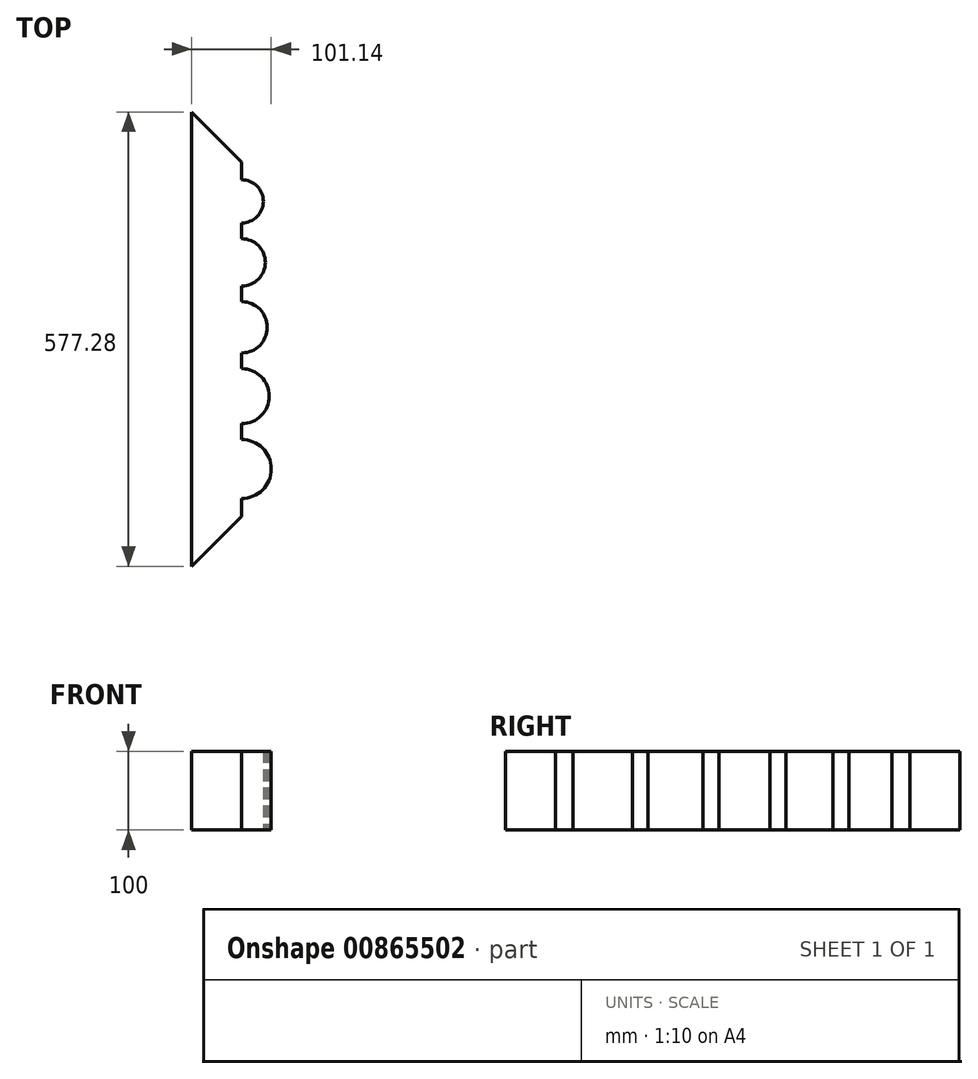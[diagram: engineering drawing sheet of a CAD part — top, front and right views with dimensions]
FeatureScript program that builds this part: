
annotation { "Feature Type Name" : "Feature", "Feature Type Description" : "" }
export const myFeature = defineFeature(function(context is Context, id is Id, definition is map)
    precondition{}
    {
        {
            var Q0;
            Q0=qCreatedBy(makeId("Top.planeOp"),FACE);
            var sketch = newSketch(context, id + "F0", { "sketchPlane" : qUnion([Q0])});
            skLineSegment(sketch, "E0.bottom", {"start": v(0, 0) * mm, "end": v(450, 0) * mm});
            skLineSegment(sketch, "E0.top", {"start": v(0, -450) * mm, "end": v(450, -450) * mm});
            skLineSegment(sketch, "E0.left", {"start": v(0, 0) * mm, "end": v(0, -450) * mm});
            skLineSegment(sketch, "E0.right", {"start": v(450, 0) * mm, "end": v(450, -450) * mm});
            skCircle(sketch, "E1", {"center": v(32.5, 0) * mm, "radius": 7.5 * mm});
            skCircle(sketch, "E2", {"center": v(70, 0) * mm, "radius": 10 * mm});
            skCircle(sketch, "E3", {"center": v(112.5, 0) * mm, "radius": 12.5 * mm});
            skCircle(sketch, "E4", {"center": v(212.5, 0) * mm, "radius": 17.5 * mm});
            skCircle(sketch, "E5", {"center": v(270, 0) * mm, "radius": 20 * mm});
            skPoint(sketch, "E6", {"position": v(0, -225) * mm});
            skCircle(sketch, "E7", {"center": v(160, 0) * mm, "radius": 15 * mm});
            skCircle(sketch, "E8", {"center": v(332.5, 0) * mm, "radius": 22.5 * mm});
            skCircle(sketch, "E9", {"center": v(400, 0) * mm, "radius": 25 * mm});
            skCircle(sketch, "E10", {"center": v(0, -50) * mm, "radius": 27.5 * mm});
            skCircle(sketch, "E11", {"center": v(0, -127.5) * mm, "radius": 30 * mm});
            skCircle(sketch, "E12", {"center": v(0, -210) * mm, "radius": 32.5 * mm});
            skCircle(sketch, "E13", {"center": v(0, -297.5) * mm, "radius": 35 * mm});
            skCircle(sketch, "E14", {"center": v(0, -390) * mm, "radius": 37.5 * mm});
            skCircle(sketch, "E15.cCircle", {"center": v(450, -45) * mm, "radius": 20 * mm, "construction": true});
            skLineSegment(sketch, "E15.0", {"start": v(450, -65) * mm, "end": v(432.68, -55) * mm});
            skLineSegment(sketch, "E15.1", {"start": v(432.68, -55) * mm, "end": v(432.68, -35) * mm});
            skLineSegment(sketch, "E15.2", {"start": v(432.68, -35) * mm, "end": v(450, -25) * mm});
            skLineSegment(sketch, "E15.3", {"start": v(450, -25) * mm, "end": v(467.32, -35) * mm});
            skLineSegment(sketch, "E15.4", {"start": v(467.32, -35) * mm, "end": v(467.32, -55) * mm});
            skLineSegment(sketch, "E15.5", {"start": v(467.32, -55) * mm, "end": v(450, -65) * mm});
            skCircle(sketch, "E16.cCircle", {"center": v(450, -120) * mm, "radius": 34.64 * mm, "construction": true});
            skLineSegment(sketch, "E16.0", {"start": v(420.17, -137.61) * mm, "end": v(419.83, -102.97) * mm});
            skLineSegment(sketch, "E16.1", {"start": v(419.83, -102.97) * mm, "end": v(449.66, -85.36) * mm});
            skLineSegment(sketch, "E16.2", {"start": v(449.66, -85.36) * mm, "end": v(479.83, -102.39) * mm});
            skLineSegment(sketch, "E16.3", {"start": v(479.83, -102.39) * mm, "end": v(480.17, -137.03) * mm});
            skLineSegment(sketch, "E16.4", {"start": v(480.17, -137.03) * mm, "end": v(450.34, -154.64) * mm});
            skLineSegment(sketch, "E16.5", {"start": v(450.34, -154.64) * mm, "end": v(420.17, -137.61) * mm});
            skCircle(sketch, "E17.cCircle", {"center": v(450, -225) * mm, "radius": 46.19 * mm, "construction": true});
            skLineSegment(sketch, "E17.0", {"start": v(410.35, -248.7) * mm, "end": v(409.66, -202.51) * mm});
            skLineSegment(sketch, "E17.1", {"start": v(409.66, -202.51) * mm, "end": v(449.3, -178.82) * mm});
            skLineSegment(sketch, "E17.2", {"start": v(449.3, -178.82) * mm, "end": v(489.65, -201.3) * mm});
            skLineSegment(sketch, "E17.3", {"start": v(489.65, -201.3) * mm, "end": v(490.34, -247.49) * mm});
            skLineSegment(sketch, "E17.4", {"start": v(490.34, -247.49) * mm, "end": v(450.7, -271.18) * mm});
            skLineSegment(sketch, "E17.5", {"start": v(450.7, -271.18) * mm, "end": v(410.35, -248.7) * mm});
            skCircle(sketch, "E18.cCircle", {"center": v(450, -360) * mm, "radius": 57.74 * mm, "construction": true});
            skLineSegment(sketch, "E18.0", {"start": v(400.24, -330.72) * mm, "end": v(450.48, -302.27) * mm});
            skLineSegment(sketch, "E18.1", {"start": v(450.48, -302.27) * mm, "end": v(500.24, -331.55) * mm});
            skLineSegment(sketch, "E18.2", {"start": v(500.24, -331.55) * mm, "end": v(499.76, -389.28) * mm});
            skLineSegment(sketch, "E18.3", {"start": v(499.76, -389.28) * mm, "end": v(449.52, -417.73) * mm});
            skLineSegment(sketch, "E18.4", {"start": v(449.52, -417.73) * mm, "end": v(399.76, -388.45) * mm});
            skLineSegment(sketch, "E18.5", {"start": v(399.76, -388.45) * mm, "end": v(400.24, -330.72) * mm});
            skLineSegment(sketch, "E19", {"start": v(420, -450) * mm, "end": v(412.5, -437) * mm});
            skLineSegment(sketch, "E20", {"start": v(412.5, -437) * mm, "end": v(405, -450) * mm});
            skLineSegment(sketch, "E21", {"start": v(420, -450) * mm, "end": v(405, -450) * mm});
            skLineSegment(sketch, "E22", {"start": v(375, -450) * mm, "end": v(362.5, -428.35) * mm});
            skLineSegment(sketch, "E23", {"start": v(362.5, -428.35) * mm, "end": v(350, -450) * mm});
            skLineSegment(sketch, "E24", {"start": v(350, -450) * mm, "end": v(375, -450) * mm});
            skLineSegment(sketch, "E25", {"start": v(320, -450) * mm, "end": v(305, -424.02) * mm});
            skLineSegment(sketch, "E26", {"start": v(305, -424.02) * mm, "end": v(290, -450) * mm});
            skLineSegment(sketch, "E27", {"start": v(290, -450) * mm, "end": v(320, -450) * mm});
            skLineSegment(sketch, "E28", {"start": v(260, -450) * mm, "end": v(220, -450) * mm});
            skLineSegment(sketch, "E29", {"start": v(220, -450) * mm, "end": v(240, -415.36) * mm});
            skLineSegment(sketch, "E30", {"start": v(240, -415.36) * mm, "end": v(260, -450) * mm});
            skLineSegment(sketch, "E31", {"start": v(190, -450) * mm, "end": v(140, -450) * mm});
            skLineSegment(sketch, "E32", {"start": v(140, -450) * mm, "end": v(165, -406.7) * mm});
            skLineSegment(sketch, "E33", {"start": v(165, -406.7) * mm, "end": v(190, -450) * mm});
            skLineSegment(sketch, "E34", {"start": v(110, -450) * mm, "end": v(50, -450) * mm});
            skLineSegment(sketch, "E35", {"start": v(50, -450) * mm, "end": v(80, -398.04) * mm});
            skLineSegment(sketch, "E36", {"start": v(80, -398.04) * mm, "end": v(110, -450) * mm});
            skCircle(sketch, "E37", {"center": v(366.86, -63.19) * mm, "radius": 8.5 * mm});
            skCircle(sketch, "E38", {"center": v(306.86, -63.19) * mm, "radius": 11.5 * mm});
            skCircle(sketch, "E39", {"center": v(237.86, -63.19) * mm, "radius": 17.5 * mm});
            skCircle(sketch, "E40", {"center": v(172.86, -63.19) * mm, "radius": 22.5 * mm});
            skCircle(sketch, "E41", {"center": v(90.36, -63.19) * mm, "radius": 30 * mm});
            skPoint(sketch, "E42.cornerSnap0", {"position": v(400, -359.59) * mm});
            skEllipse(sketch, "E43", {"center": v(355, -158.3) * mm, "majorRadius": 69.57 * mm, "minorRadius": 24.91 * mm, "majorAxis": v(0, -1)});
            skEllipse(sketch, "E44", {"center": v(255, -158.3) * mm, "majorRadius": 57.98 * mm, "minorRadius": 25.3 * mm, "majorAxis": v(0, -1)});
            skEllipse(sketch, "E45", {"center": v(160, -158.3) * mm, "majorRadius": 47.06 * mm, "minorRadius": 19.98 * mm, "majorAxis": v(0, -1)});
            skEllipse(sketch, "E46", {"center": v(75, -158.3) * mm, "majorRadius": 42.97 * mm, "minorRadius": 16.37 * mm, "majorAxis": v(0, -1)});
            skLineSegment(sketch, "E47.bottom", {"start": v(132.9, -316.06) * mm, "end": v(52.9, -316.06) * mm});
            skLineSegment(sketch, "E47.top", {"start": v(132.9, -236.06) * mm, "end": v(52.9, -236.06) * mm});
            skLineSegment(sketch, "E47.left", {"start": v(132.9, -316.06) * mm, "end": v(132.9, -236.06) * mm});
            skLineSegment(sketch, "E47.right", {"start": v(52.9, -316.06) * mm, "end": v(52.9, -236.06) * mm});
            skPoint(sketch, "E47.middle", {"position": v(92.9, -276.06) * mm});
            skLineSegment(sketch, "E48.bottom", {"start": v(232.94, -306.06) * mm, "end": v(172.94, -306.06) * mm});
            skLineSegment(sketch, "E48.top", {"start": v(232.94, -246.06) * mm, "end": v(172.94, -246.06) * mm});
            skLineSegment(sketch, "E48.left", {"start": v(232.94, -306.06) * mm, "end": v(232.94, -246.06) * mm});
            skLineSegment(sketch, "E48.right", {"start": v(172.94, -306.06) * mm, "end": v(172.94, -246.06) * mm});
            skPoint(sketch, "E48.middle", {"position": v(202.94, -276.06) * mm});
            skLineSegment(sketch, "E49.bottom", {"start": v(312.28, -296.06) * mm, "end": v(272.28, -296.06) * mm});
            skLineSegment(sketch, "E49.top", {"start": v(312.28, -256.06) * mm, "end": v(272.28, -256.06) * mm});
            skLineSegment(sketch, "E49.left", {"start": v(312.28, -296.06) * mm, "end": v(312.28, -256.06) * mm});
            skLineSegment(sketch, "E49.right", {"start": v(272.28, -296.06) * mm, "end": v(272.28, -256.06) * mm});
            skPoint(sketch, "E49.middle", {"position": v(292.28, -276.06) * mm});
            skLineSegment(sketch, "E50.bottom", {"start": v(372.3, -286.06) * mm, "end": v(352.3, -286.06) * mm});
            skLineSegment(sketch, "E50.top", {"start": v(372.3, -266.06) * mm, "end": v(352.3, -266.06) * mm});
            skLineSegment(sketch, "E50.left", {"start": v(372.3, -286.06) * mm, "end": v(372.3, -266.06) * mm});
            skLineSegment(sketch, "E50.right", {"start": v(352.3, -286.06) * mm, "end": v(352.3, -266.06) * mm});
            skPoint(sketch, "E50.middle", {"position": v(362.3, -276.06) * mm});
            skLineSegment(sketch, "E51.bottom", {"start": v(80, -382.47) * mm, "end": v(60, -382.47) * mm});
            skLineSegment(sketch, "E51.top", {"start": v(80, -372.47) * mm, "end": v(60, -372.47) * mm});
            skLineSegment(sketch, "E51.left", {"start": v(80, -382.47) * mm, "end": v(80, -372.47) * mm});
            skLineSegment(sketch, "E51.right", {"start": v(60, -382.47) * mm, "end": v(60, -372.47) * mm});
            skPoint(sketch, "E51.middle", {"position": v(70, -377.47) * mm});
            skLineSegment(sketch, "E52.bottom", {"start": v(110, -387.47) * mm, "end": v(150, -387.47) * mm});
            skLineSegment(sketch, "E52.top", {"start": v(110, -367.47) * mm, "end": v(150, -367.47) * mm});
            skLineSegment(sketch, "E52.left", {"start": v(110, -387.47) * mm, "end": v(110, -367.47) * mm});
            skLineSegment(sketch, "E52.right", {"start": v(150, -387.47) * mm, "end": v(150, -367.47) * mm});
            skPoint(sketch, "E52.middle", {"position": v(130, -377.47) * mm});
            skLineSegment(sketch, "E53.bottom", {"start": v(190, -392.47) * mm, "end": v(250, -392.47) * mm});
            skLineSegment(sketch, "E53.top", {"start": v(190, -362.47) * mm, "end": v(250, -362.47) * mm});
            skLineSegment(sketch, "E53.left", {"start": v(190, -392.47) * mm, "end": v(190, -362.47) * mm});
            skLineSegment(sketch, "E53.right", {"start": v(250, -392.47) * mm, "end": v(250, -362.47) * mm});
            skPoint(sketch, "E53.middle", {"position": v(220, -377.47) * mm});
            skLineSegment(sketch, "E54.bottom", {"start": v(375, -397.47) * mm, "end": v(295, -397.47) * mm});
            skLineSegment(sketch, "E54.top", {"start": v(375, -357.47) * mm, "end": v(295, -357.47) * mm});
            skLineSegment(sketch, "E54.left", {"start": v(375, -397.47) * mm, "end": v(375, -357.47) * mm});
            skLineSegment(sketch, "E54.right", {"start": v(295, -397.47) * mm, "end": v(295, -357.47) * mm});
            skPoint(sketch, "E54.middle", {"position": v(335, -377.47) * mm});
            skLineSegment(sketch, "E55", {"start": v(0, 0) * mm, "end": v(-63.64, 63.64) * mm});
            skLineSegment(sketch, "E56", {"start": v(-63.64, 63.64) * mm, "end": v(513.64, 63.64) * mm});
            skLineSegment(sketch, "E57", {"start": v(513.64, 63.64) * mm, "end": v(450, 0) * mm});
            skLineSegment(sketch, "E58", {"start": v(513.64, 63.64) * mm, "end": v(513.64, -513.64) * mm});
            skLineSegment(sketch, "E59", {"start": v(513.64, -513.64) * mm, "end": v(450, -450) * mm});
            skLineSegment(sketch, "E60", {"start": v(-63.64, 63.64) * mm, "end": v(-63.64, -513.64) * mm});
            skLineSegment(sketch, "E61", {"start": v(-63.64, -513.64) * mm, "end": v(0, -450) * mm});
            skLineSegment(sketch, "E62", {"start": v(-63.64, -513.64) * mm, "end": v(513.64, -513.64) * mm});
            skSolve(sketch);
        }
        {
            var Q0;
            {var subQ17=sQuery(id+"F0.wireOp",EDGE,"E55");Q0=makeQuery(id+"F0.imprint","IMPRINT",FACE,{"disambiguationData":[TD([[makeQuery(id+"F0.imprint","IMPRINT",EDGE,{"derivedFrom":subQ17}),1.0]])]});}
            var Q1;
            {var subQ0=sQuery(id+"F0.wireOp",EDGE,"E10");var subQ1=sQuery(id+"F0.wireOp",EDGE,"E0.left");var subQ2=makeQuery(id+"F0.imprint","INTERSECT",VERTEX,{"disambiguationData":[OD(0.0)],"derivedFrom":[subQ1,subQ0]});Q1=makeQuery(id+"F0.imprint","IMPRINT",FACE,{"disambiguationData":[TD([[makeQuery(id+"F0.imprint","IMPRINT",EDGE,{"disambiguationData":[TD([[subQ2,-1.0]])],"derivedFrom":subQ1}),-1.0]])]});}
            var Q2;
            {var subQ0=sQuery(id+"F0.wireOp",EDGE,"E10");var subQ1=sQuery(id+"F0.wireOp",EDGE,"E0.left");var subQ2=makeQuery(id+"F0.imprint","INTERSECT",VERTEX,{"disambiguationData":[OD(0.0)],"derivedFrom":[subQ1,subQ0]});Q2=makeQuery(id+"F0.imprint","IMPRINT",FACE,{"disambiguationData":[TD([[makeQuery(id+"F0.imprint","IMPRINT",EDGE,{"disambiguationData":[TD([[subQ2,-1.0]])],"derivedFrom":subQ1}),1.0]])]});}
            var Q3;
            {var subQ0=sQuery(id+"F0.wireOp",EDGE,"E11");var subQ1=sQuery(id+"F0.wireOp",EDGE,"E0.left");var subQ2=makeQuery(id+"F0.imprint","INTERSECT",VERTEX,{"disambiguationData":[OD(0.0)],"derivedFrom":[subQ1,subQ0]});Q3=makeQuery(id+"F0.imprint","IMPRINT",FACE,{"disambiguationData":[TD([[makeQuery(id+"F0.imprint","IMPRINT",EDGE,{"disambiguationData":[TD([[subQ2,-1.0]])],"derivedFrom":subQ1}),1.0]])]});}
            var Q4;
            {var subQ0=sQuery(id+"F0.wireOp",EDGE,"E11");var subQ1=sQuery(id+"F0.wireOp",EDGE,"E0.left");var subQ2=makeQuery(id+"F0.imprint","INTERSECT",VERTEX,{"disambiguationData":[OD(0.0)],"derivedFrom":[subQ1,subQ0]});Q4=makeQuery(id+"F0.imprint","IMPRINT",FACE,{"disambiguationData":[TD([[makeQuery(id+"F0.imprint","IMPRINT",EDGE,{"disambiguationData":[TD([[subQ2,-1.0]])],"derivedFrom":subQ1}),-1.0]])]});}
            var Q5;
            {var subQ0=sQuery(id+"F0.wireOp",EDGE,"E12");var subQ1=sQuery(id+"F0.wireOp",EDGE,"E0.left");var subQ2=makeQuery(id+"F0.imprint","INTERSECT",VERTEX,{"disambiguationData":[OD(0.0)],"derivedFrom":[subQ1,subQ0]});Q5=makeQuery(id+"F0.imprint","IMPRINT",FACE,{"disambiguationData":[TD([[makeQuery(id+"F0.imprint","IMPRINT",EDGE,{"disambiguationData":[TD([[subQ2,-1.0]])],"derivedFrom":subQ1}),-1.0]])]});}
            var Q6;
            {var subQ0=sQuery(id+"F0.wireOp",EDGE,"E12");var subQ1=sQuery(id+"F0.wireOp",EDGE,"E0.left");var subQ2=makeQuery(id+"F0.imprint","INTERSECT",VERTEX,{"disambiguationData":[OD(0.0)],"derivedFrom":[subQ1,subQ0]});Q6=makeQuery(id+"F0.imprint","IMPRINT",FACE,{"disambiguationData":[TD([[makeQuery(id+"F0.imprint","IMPRINT",EDGE,{"disambiguationData":[TD([[subQ2,-1.0]])],"derivedFrom":subQ1}),1.0]])]});}
            var Q7;
            {var subQ0=sQuery(id+"F0.wireOp",EDGE,"E13");var subQ1=sQuery(id+"F0.wireOp",EDGE,"E0.left");var subQ2=makeQuery(id+"F0.imprint","INTERSECT",VERTEX,{"disambiguationData":[OD(0.0)],"derivedFrom":[subQ1,subQ0]});Q7=makeQuery(id+"F0.imprint","IMPRINT",FACE,{"disambiguationData":[TD([[makeQuery(id+"F0.imprint","IMPRINT",EDGE,{"disambiguationData":[TD([[subQ2,-1.0]])],"derivedFrom":subQ1}),1.0]])]});}
            var Q8;
            {var subQ0=sQuery(id+"F0.wireOp",EDGE,"E13");var subQ1=sQuery(id+"F0.wireOp",EDGE,"E0.left");var subQ2=makeQuery(id+"F0.imprint","INTERSECT",VERTEX,{"disambiguationData":[OD(0.0)],"derivedFrom":[subQ1,subQ0]});Q8=makeQuery(id+"F0.imprint","IMPRINT",FACE,{"disambiguationData":[TD([[makeQuery(id+"F0.imprint","IMPRINT",EDGE,{"disambiguationData":[TD([[subQ2,-1.0]])],"derivedFrom":subQ1}),-1.0]])]});}
            var Q9;
            {var subQ0=sQuery(id+"F0.wireOp",EDGE,"E14");var subQ1=sQuery(id+"F0.wireOp",EDGE,"E0.left");var subQ2=makeQuery(id+"F0.imprint","INTERSECT",VERTEX,{"disambiguationData":[OD(0.0)],"derivedFrom":[subQ1,subQ0]});Q9=makeQuery(id+"F0.imprint","IMPRINT",FACE,{"disambiguationData":[TD([[makeQuery(id+"F0.imprint","IMPRINT",EDGE,{"disambiguationData":[TD([[subQ2,-1.0]])],"derivedFrom":subQ1}),-1.0]])]});}
            var Q10;
            {var subQ0=sQuery(id+"F0.wireOp",EDGE,"E14");var subQ1=sQuery(id+"F0.wireOp",EDGE,"E0.left");var subQ2=makeQuery(id+"F0.imprint","INTERSECT",VERTEX,{"disambiguationData":[OD(0.0)],"derivedFrom":[subQ1,subQ0]});Q10=makeQuery(id+"F0.imprint","IMPRINT",FACE,{"disambiguationData":[TD([[makeQuery(id+"F0.imprint","IMPRINT",EDGE,{"disambiguationData":[TD([[subQ2,-1.0]])],"derivedFrom":subQ1}),1.0]])]});}
            extrude(context, id + "F1", {"entities" : qUnion([Q0, Q1, Q2, Q3, Q4, Q5, Q6, Q7, Q8, Q9, Q10]), "depth" : 100 * mm, "offsetDistance" : 25 * mm});
        }
    });
